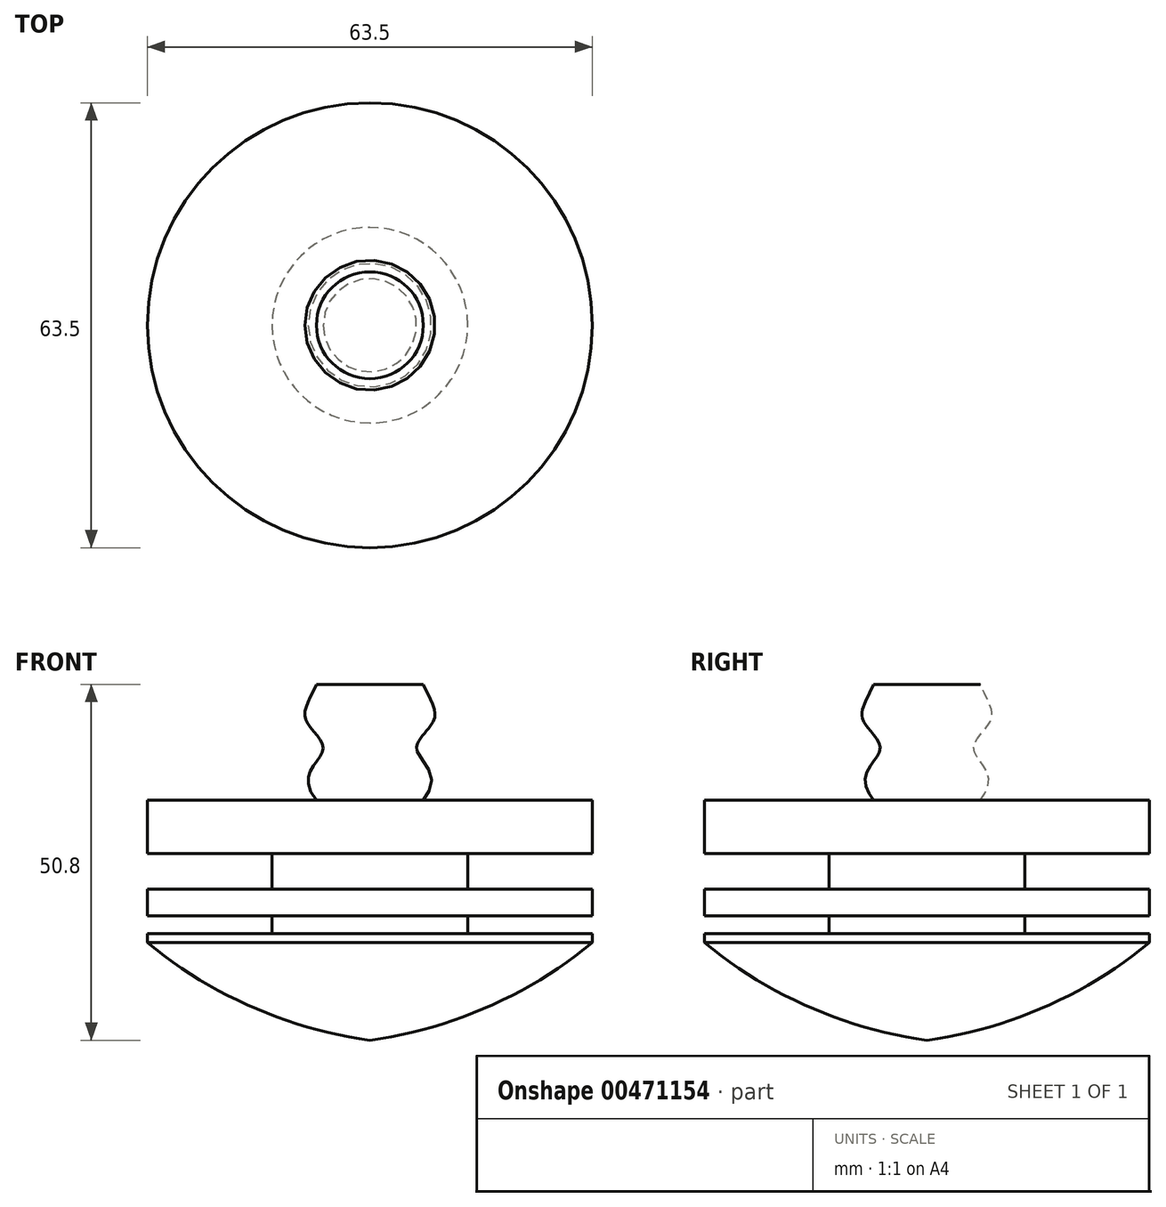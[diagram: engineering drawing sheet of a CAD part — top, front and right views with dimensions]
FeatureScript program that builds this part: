
annotation { "Feature Type Name" : "Feature", "Feature Type Description" : "" }
export const myFeature = defineFeature(function(context is Context, id is Id, definition is map)
    precondition{}
    {
        {
            var Q0;
            Q0=qCreatedBy(makeId("Front.planeOp"),FACE);
            var sketch = newSketch(context, id + "F0", { "sketchPlane" : qUnion([Q0])});
            skLineSegment(sketch, "E0", {"start": v(31.75, 21.57) * mm, "end": v(31.75, 17.76) * mm});
            skArc(sketch, "E1", {"start": v(0, 0) * mm, "mid": v(16.85, 4.76) * mm, "end": v(31.75, 13.95) * mm});
            skLineSegment(sketch, "E2", {"start": v(31.75, 13.95) * mm, "end": v(31.75, 15.22) * mm});
            skLineSegment(sketch, "E3", {"start": v(31.75, 15.22) * mm, "end": v(13.96, 15.22) * mm});
            skLineSegment(sketch, "E4.0", {"start": v(31.75, 17.76) * mm, "end": v(13.96, 17.76) * mm});
            skLineSegment(sketch, "E5.0", {"start": v(31.75, 21.57) * mm, "end": v(13.96, 21.57) * mm});
            skLineSegment(sketch, "E6.0", {"start": v(31.75, 26.65) * mm, "end": v(13.96, 26.65) * mm});
            skLineSegment(sketch, "E7.trimOffspring", {"start": v(31.75, 15.22) * mm, "end": v(31.75, 13.95) * mm});
            skLineSegment(sketch, "E8", {"start": v(13.96, 21.57) * mm, "end": v(13.96, 26.65) * mm});
            skLineSegment(sketch, "E9", {"start": v(13.96, 17.76) * mm, "end": v(13.96, 15.22) * mm});
            skLineSegment(sketch, "E10", {"start": v(31.75, 26.65) * mm, "end": v(31.75, 34.27) * mm});
            skLineSegment(sketch, "E11", {"start": v(0, 0) * mm, "end": v(0, 50.8) * mm});
            skLineSegment(sketch, "E12", {"start": v(0, 50.8) * mm, "end": v(7.62, 50.8) * mm});
            skLineSegment(sketch, "E13", {"start": v(31.75, 34.27) * mm, "end": v(7.62, 34.27) * mm});
            skFitSpline(sketch, "E14", {"points": [v(7.62, 50.8) * mm, v(9.06, 45.52) * mm, v(6.67, 41.48) * mm, v(7.62, 34.27) * mm], "startDerivative": vector(10.85, -23.4) * mm, "endDerivative": vector(-24.34, -30.13) * mm});
            skSolve(sketch);
        }
        {
            var Q0;
            Q0=makeQuery(id+"F0.imprint","IMPRINT",FACE,{"disambiguationData":[TD([[makeQuery(id+"F0.imprint","IMPRINT",EDGE,{"derivedFrom":sQuery(id+"F0.wireOp",EDGE,"E0")}),-1.0]])]});
            var Q1;
            Q1=sQuery(id+"F0.wireOp",EDGE,"E11");
            revolve(context, id + "F1", {"entities" : qUnion([Q0]), "axis" : qUnion([Q1]), "revolveType" : RevolveType.FULL});
        }
    });
